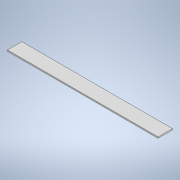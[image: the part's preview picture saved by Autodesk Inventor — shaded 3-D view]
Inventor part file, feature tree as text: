
AUTODESK INVENTOR PART (.ipt)
format: ipt  version: 2022 (Build 260153000, 153)  size: 93,184 bytes
history: native  units: mm
features: extrude x1, sketch x1
ambient origin geometry x8: Origin, YZ Plane, XZ Plane, XY Plane, X Axis, Y Axis, Z Axis, Center Point
bodies: Solid1 (feature_tree)
feature tree (2):
  extrude  "Extrusion1"  Depth=10.0mm
  sketch  "Sketch1"  dims[d0=105.0mm d1=10.0mm d2=0.9mm d3=0.0mm]
